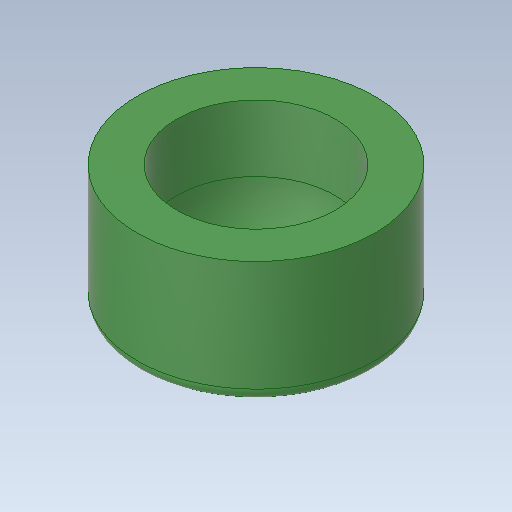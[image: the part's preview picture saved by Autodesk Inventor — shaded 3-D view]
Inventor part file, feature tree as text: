
AUTODESK INVENTOR PART (.ipt)
format: ipt  version: 2020.1 (Build 241239000, 239)  size: 148,480 bytes
history: native  units: mm
features: other x1, revolve x1, fillet x1, sketch x1
ambient origin geometry x8: Origin, YZ Plane, XZ Plane, XY Plane, X Axis, Y Axis, Z Axis, Center Point
bodies: Body1 (feature_tree)
feature tree (4):
  other  "Твердое тело1"
  revolve  "Вращение1"
  fillet  "Сопряжение1"  Radius=18.0mm
  sketch  "Эскиз1"
